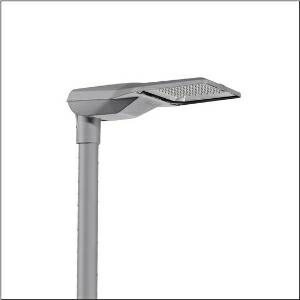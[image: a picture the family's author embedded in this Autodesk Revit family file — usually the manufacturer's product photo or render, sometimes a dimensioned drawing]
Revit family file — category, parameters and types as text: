
# Revit family: streetlight_sl_21_midi___st1_5a_5xe7p33a08mb_920b
name_source: partatom
category: Lighting Fixtures
units: mm (PartAtom-declared; Revit-internal decimal feet)

## family parameters
Cut with Voids When Loaded = No
Host = Face
Light Source = No
Part Type = Normal
Room Calculation Point = No
Round Connector Dimension = Use Diameter
Shared = No

## types (1)
- --- (1 x LED, 17960 lm, 136 W, 3000K)
    Apparent Load = 136 VA
    CIE Flux Codes = 22 53 95 100 100
    Color Rendering = 70
    Color Temperature = 3000K
    Default Elevation = 1800 mm
    Description = Streetlight SL 21 midi, mast luminaire, primary light control with lens, of PMMA, primary optical cover: cover, of toughened safety glass, transparent, light distribution: ST1.5a, light emission: direct distribution, primary light characteristic: asymmetric, installation type: post-top, side-entry, LED, 3G 1.5mm², High Power LED, rated luminous flux: 17.960lm, luminous efficacy: 132lm/W, light colour: 730, colour temperature: 3000K, control gear: Easy, control: overheat protection, constant luminous flux control, time-dependent luminous flux control, flexible luminous flux parameterisation, mains connection: 220..240V, AC, 50/60Hz, connection cable pre-assembled, cable length: 12,5m, wiring characteristics: H07RN-F, start of lifetime: 136W, end of service life: 142W, reduction: 61W, luminaire housing, of diecast aluminium, powder-coated, Siteco® metallic grey (DB 702S), corrosivity category C5 mid according to DIN EN ISO 12944, please order mast flange separately, inclination adjustable: 0°, 5°, 10°, 15°, sealing non-destructively replaceable, multi-level sealing system, length: 644mm, width: 335mm, height: 110mm, mast flange for spigot size: 42mm (side-entry): 5XC10008XM4, 60/48mm (side-entry/post-top): 5XC10108XM2, 76/60mm (side-entry/post-top): 5XC10108XM1, mounting height: 4..8m, protection rating (complete): IP66, insulation class (complete): insulation class II (safety insulation), certification: CE, ENEC, ENEC+, VDE, impact resistance: IK10, permissible operating ambient temperature for outdoor applications: -40..+50°C, standard-compliant lighting for roads and squares, packaging unit: 1 piece

Light Distribution: ST1.5a
    Height = 111 mm
    Lamp = 1 x LED
    Lamp Light Flux = 17960 lm
    Lamp Power = 136 W
    Lamp count = 1
    Length = 644 mm
    Luminous efficacy = 132 lm/W
    Manufacturer = Siteco
    ModVariant = No
    Model = 5XE7P33A08MB
    Number of Poles = 1
    OnlyDefault = Yes
    Power Factor = 1
    Product Name = Streetlight SL 21 midi | ST1.5a
    Product group = mast luminaire | pylon top
    ProductGroupID = 6100
    Protection Class = Protection class II
    Protection Degree = IP 66
    RLX_Detail_Level = 1
    RLX_Emergency_Light_Flux = 0 lm
    RLX_Emergency_Type = 0
    RLX_Emergency_Type_DB = No
    RlxData = <blob elided: 30285 chars, md5=d446613c>
    Socket = socket
    Standby Power = 0 W
    System Light Flux = 17960 lm
    System Power = 136 W
    Type Comments = factory setting: luminous flux: 100 % | Output Level: 100 % | 695 mA
    Type Image = l_1004298.jpg
    URL = http://relux.com
    VarID = @adj_197415
    Voltage = 0 V
    Weight = 0.00 kg
    Width = 336 mm

## geometry (parser evidence)
native form markers: Blend x4, Sweep x10
no freeform markers — native parametric forms only
